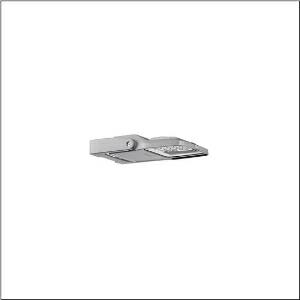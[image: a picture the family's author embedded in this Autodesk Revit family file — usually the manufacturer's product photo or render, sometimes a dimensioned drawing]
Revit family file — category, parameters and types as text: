
# Revit family: floodlight_fl_21_iq_micro___pl33t_5xa7761a2f2a_98c0
name_source: partatom
category: Lighting Fixtures
units: mm (PartAtom-declared; Revit-internal decimal feet)

## family parameters
Cut with Voids When Loaded = No
Host = Face
Light Source = No
Part Type = Normal
Room Calculation Point = No
Round Connector Dimension = Use Diameter
Shared = No

## types (1)
- --- (1 x LED, 2930 lm, 23.1 W, 3000K)
    Apparent Load = 23 VA
    CIE Flux Codes = 26 75 99 100 100
    Color Rendering = 70
    Color Temperature = 3000K
    Default Elevation = 1800 mm
    Description = Floodlight FL 21 iQ micro, floodlight, primary light control with lens, of PMMA, primary optical cover: protective disc, of toughened safety glass, transparent, light distribution: PL33T, light emission: direct distribution, installation type: surface-mounted, LED, High Power LED, rated luminous flux: 2.930lm, luminous efficacy: 127lm/W, light colour: 730, colour temperature: 3000K, control gear: iQ Comfort/DALI, control: optimised constant luminous flux control (CLO 2.0), Desk-Remote (wireless, voltage-free reading and setting of iQ features in the workshop via application-optimized NFC function/RFID function), Light-Fading, Smart-Wire, Night-Set, Lumen-Switch, Temp-Guard, Auto-Match, with terminal, 6-pole, mains connection: 220..240V, AC, 50/60Hz, start of lifetime: 23W, end of service life: 24W, reduction: 11W, luminaire housing, of diecast aluminium, powder-coated, Siteco® metallic grey (DB 702S), corrosivity category C5 mid according to DIN EN ISO 12944, suitable for swimming pools, chlorine-resistant, sealing non-destructively replaceable, design bracket, of diecast aluminium, powder-coated, Siteco® metallic grey (DB 702S), protection rating (complete): IP66, insulation class (complete): insulation class II (safety insulation), certification: CE, ENEC, VDE, protection symbol: D, impact resistance: IK07, permissible operating ambient temperature: -40..+40°C, permissible operating ambient temperature for outdoor applications: -40..+50°C, standard: DIN EN 12944, LABS conformity tested according to VDMA 24364:2018-05, packaging unit: 1 piece

Light Distribution: PL33T
    Height = 65 mm
    Lamp = 1 x LED
    Lamp Light Flux = 2930 lm
    Lamp Power = 23.1 W
    Lamp count = 1
    Length = 312 mm
    Luminous efficacy = 127 lm/W
    Manufacturer = Siteco
    ModVariant = No
    Model = 5XA7761A2F2A
    Mounting Place = Wall
    Mounting Type = Surface mounted
    Number of Poles = 1
    OnlyDefault = Yes
    Power Factor = 1
    Product Name = Floodlight FL 21 iQ micro | PL33T
    Product group = floodlight | wall mounted
    ProductGroupID = 2001
    Protection Class = Protection class II
    Protection Degree = IP 66
    RLX_Detail_Level = 1
    RLX_Emergency_Light_Flux = 0 lm
    RLX_Emergency_Type = 0
    RLX_Emergency_Type_DB = No
    RlxData = <blob elided: 97401 chars, md5=0d208bc7>
    Socket = socket
    Standby Power = 0 W
    System Light Flux = 2930 lm
    System Power = 23 W
    Type Comments = factory setting: luminous flux: 100 % | dim-lin: 254 | 455 mA
    Type Image = l_1006878.jpg
    URL = http://relux.com
    VarID = @adj_148262
    Voltage = 0 V
    Weight = 0.00 kg
    Width = 230 mm

## geometry (parser evidence)
native form markers: Blend x4, Sweep x14
no freeform markers — native parametric forms only
